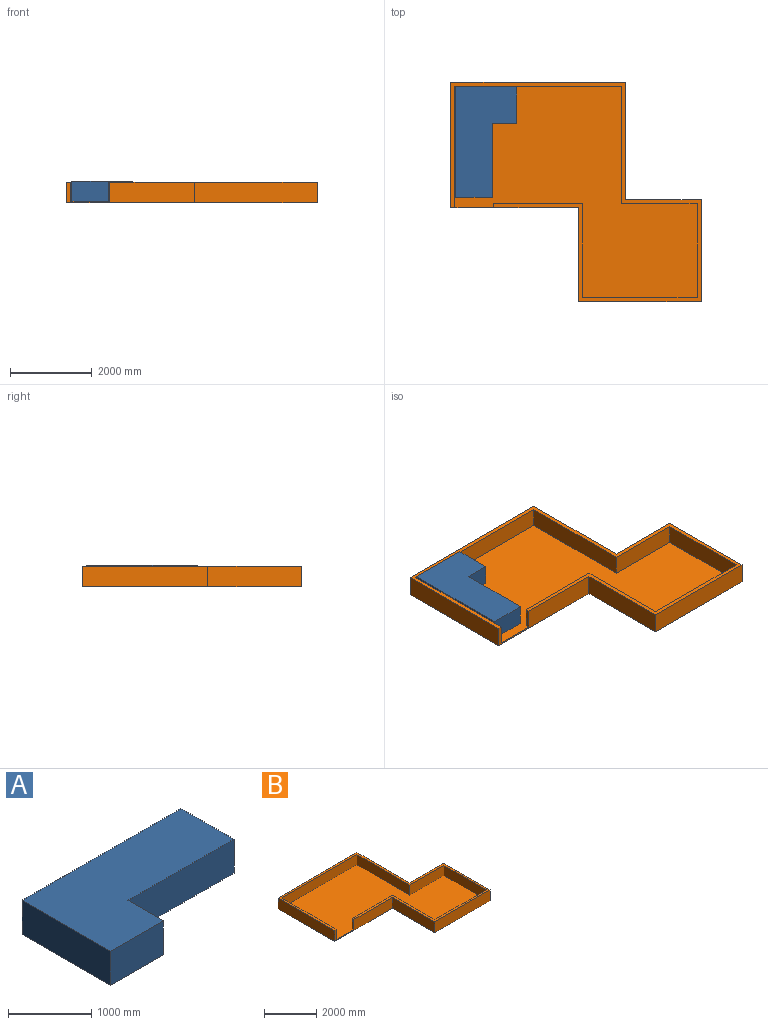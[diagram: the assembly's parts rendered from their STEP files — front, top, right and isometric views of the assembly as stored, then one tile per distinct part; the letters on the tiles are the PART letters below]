
ASSEMBLY  parts=2 mates=1
PART A: 8 faces, bbox 2700x1500x500 mm
  f0: plane 1500x500mm, normal (-1,0,0), area 750000mm2, adj f1,f5,f6,f7
  f1: plane 900x500mm, normal (0,-1,0), area 450000mm2, adj f0,f2,f6,f7
  f2: plane 600x500mm, normal (1,0,0), area 300000mm2, adj f1,f3,f6,f7
  f3: plane 1800x500mm, normal (0,-1,0), area 900000mm2, adj f2,f4,f6,f7
  f4: plane 900x500mm, normal (1,0,0), area 450000mm2, adj f3,f5,f6,f7
  f5: plane 2700x500mm, normal (0,1,0), area 1350000mm2, adj f0,f4,f6,f7
  f6: plane 2700x1500mm, normal (0,0,1), area 2970000mm2, adj f0,f1,f2,f3,f4,f5
  f7: plane 2700x1500mm, normal (0,0,-1), area 2970000mm2, adj f0,f1,f2,f3,f4,f5
PART B: 20 faces, bbox 6130x5370x510 mm
  f0: plane 2180x475mm, normal (0,1,0), area 1035500mm2, adj f1,f16,f17,f19
  f1: plane 475x100mm, normal (-1,0,0), area 47500mm2, adj f0,f9,f17,f19
  f2: plane 2300x510mm, normal (-1,0,0), area 1173000mm2, adj f3,f9,f17,f18
  f3: plane 3000x510mm, normal (0,-1,0), area 1530000mm2, adj f2,f4,f17,f18
  f4: plane 2500x510mm, normal (1,0,0), area 1275000mm2, adj f3,f5,f17,f18
  f5: plane 1850x510mm, normal (0,1,0), area 943500mm2, adj f4,f6,f17,f18
  f6: plane 2870x510mm, normal (1,0,0), area 1463700mm2, adj f5,f7,f17,f18
  f7: plane 4280x510mm, normal (0,1,0), area 2182800mm2, adj f6,f8,f17,f18
  f8: plane 3070x510mm, normal (-1,0,0), area 1565700mm2, adj f7,f9,f17,f18
  f9: plane 3130x510mm, normal (0,-1,0), area 1145050mm2, adj f1,f2,f8,f10,f17,f18,f19
  f10: plane 2970x475mm, normal (1,0,0), area 1410750mm2, adj f9,f11,f17,f19
  f11: plane 4080x475mm, normal (0,-1,0), area 1938000mm2, adj f10,f12,f17,f19
  f12: plane 2870x475mm, normal (-1,0,0), area 1363250mm2, adj f11,f13,f17,f19
  f13: plane 1850x475mm, normal (0,-1,0), area 878750mm2, adj f12,f14,f17,f19
  f14: plane 2300x475mm, normal (-1,0,0), area 1092500mm2, adj f13,f15,f17,f19
  f15: plane 2800x475mm, normal (0,1,0), area 1330000mm2, adj f14,f16,f17,f19
  f16: plane 2300x475mm, normal (1,0,0), area 1092500mm2, adj f0,f15,f17,f19
  f17: plane 6130x5370mm, normal (0,0,1), area 2165000mm2, adj f0,f1,f2,f3,f4,f5,f6,f7
  f18: plane 6130x5370mm, normal (0,0,-1), area 20409600mm2, adj f2,f3,f4,f5,f6,f7,f8,f9
  f19: plane 5930x5170mm, normal (0,0,1), area 18244600mm2, adj f0,f1,f9,f10,f11,f12,f13,f14
PLACE A rot(axis=(-0.71,0.71,0),180deg) t=(-7796.87,2827.77,-1824.6)mm
PLACE B t=(-6381.94,2479.83,-2349.6)mm
MATE planar B.f19 <-> A.f6  axis (0,0,1) through (-5913.9,1193.25,-2324.6)mm
